# Revit family: Sanitary_Showers_AXOR_04486USA-AXOR-Starck-Baton-hand-shower-2__
name_source: partatom
category: Plumbing Fixtures
revit_build: Autodesk Revit 2018 (Build: 20170223_1515(x64)
units: mm (PartAtom-declared; Revit-internal decimal feet)

## family parameters
Always vertical = No
Cut with Voids When Loaded = No
OmniClass Number = 23.31.17.19
OmniClass Title = Shower Head Fixtures
Part Type = Normal
Room Calculation Point = No
Round Connector Dimension = Use Diameter
Shared = No
Work Plane-Based = Yes

## types (6) — shared parameters
BIMobject category = Showers
Default Elevation = 1219.2 mm  [stored 4 ft]
Description = 04486USA AXOR Starck Baton hand shower 2jet 1.75 GPM
Edition number = 1
IFC Classification = Sanitary Terminal
Manufacturer = AXOR
Manufacturer name = AXOR
Material 2 = AXOR - Plastic - Gray
Model = 04486USA
OmniClass Code = 23-31 17 19
OmniClass Description = Shower Head Fixtures
Product Guid = 4f5babfe-c875-4770-ae65-c5e7d7d6d627
Product SKU = 04486USA
Product data url = https://bimobject.com
Product family = AXOR Starck
Product group = Hand showers
Product name = 04486USA AXOR Starck Baton hand shower 2jet 1.75 GPM
Product url = https://www.axor-design.com
QR code = https://bimobject.com
URL = https://www.axor-design.com
Water Inlet = 13 mm
Water Inlet Description = Water Inlet 12.7mm
Weight Net (Kg) = 160

## per-type parameters (varying)
| type | Material 1 |
| 000 Chrome | AXOR - Metal - 000 Chrome |
| 330 Polished Black Chrome | AXOR - Metal - 330 Polished Black Chrome |
| 350 Satin Black | AXOR - Metal - 350 Satin Black |
| 670 Matt Black | AXOR - Metal - 670 Matt Black |
| 820 Brushed Nickel | AXOR - Metal - 820 Brushed Nickel |
| 990 Polished Gold Optic | AXOR - Metal - 990 Polished Gold Optic |

note: [stored X ft] marks values corroborated as IEEE doubles in the binary element streams (Revit-internal decimal feet)

## geometry (parser evidence)
native form markers: Sweep x2
no freeform markers — native parametric forms only
